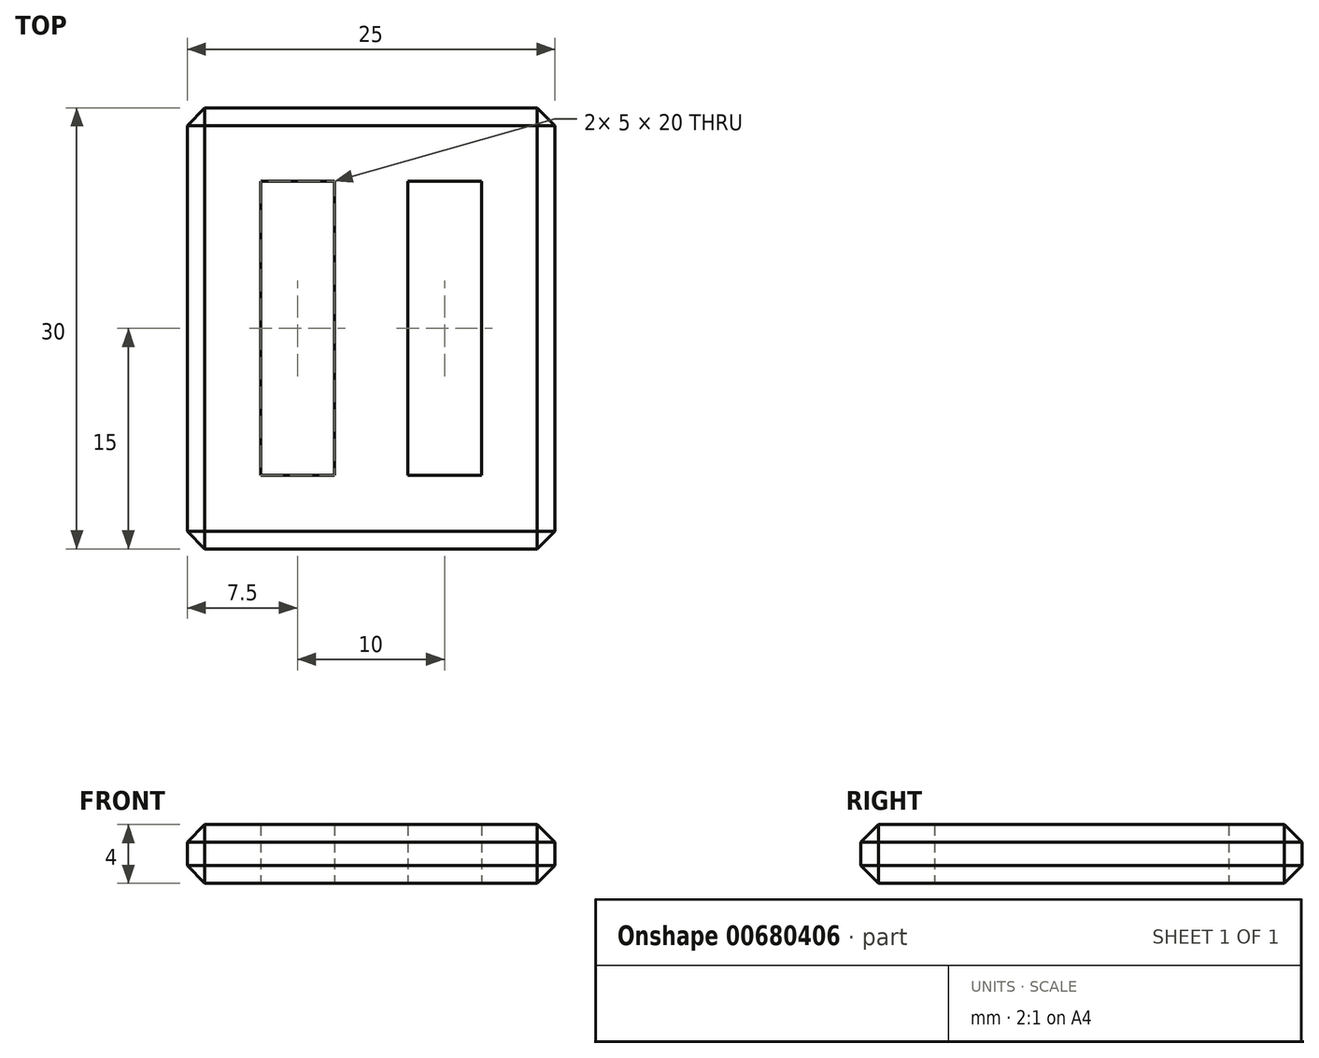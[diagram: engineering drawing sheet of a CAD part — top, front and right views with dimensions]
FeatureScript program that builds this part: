
annotation { "Feature Type Name" : "Feature", "Feature Type Description" : "" }
export const myFeature = defineFeature(function(context is Context, id is Id, definition is map)
    precondition{}
    {
        {
            var Q0;
            Q0=qCreatedBy(makeId("Top.planeOp"),FACE);
            var sketch = newSketch(context, id + "F0", { "sketchPlane" : qUnion([Q0])});
            skLineSegment(sketch, "E0.bottom", {"start": v(0, 0) * mm, "end": v(25, 0) * mm});
            skLineSegment(sketch, "E0.top", {"start": v(0, 30) * mm, "end": v(25, 30) * mm});
            skLineSegment(sketch, "E0.left", {"start": v(0, 0) * mm, "end": v(0, 30) * mm});
            skLineSegment(sketch, "E0.right", {"start": v(25, 0) * mm, "end": v(25, 30) * mm});
            skLineSegment(sketch, "E1.bottom", {"start": v(5, 5) * mm, "end": v(10, 5) * mm});
            skLineSegment(sketch, "E1.top", {"start": v(5, 25) * mm, "end": v(10, 25) * mm});
            skLineSegment(sketch, "E1.left", {"start": v(5, 5) * mm, "end": v(5, 25) * mm});
            skLineSegment(sketch, "E1.right", {"start": v(10, 5) * mm, "end": v(10, 25) * mm});
            skLineSegment(sketch, "E2.bottom", {"start": v(15, 5) * mm, "end": v(20, 5) * mm});
            skLineSegment(sketch, "E2.top", {"start": v(15, 25) * mm, "end": v(20, 25) * mm});
            skLineSegment(sketch, "E2.left", {"start": v(15, 5) * mm, "end": v(15, 25) * mm});
            skLineSegment(sketch, "E2.right", {"start": v(20, 5) * mm, "end": v(20, 25) * mm});
            skSolve(sketch);
        }
        {
            var Q0;
            Q0=makeQuery(id+"F0.imprint","IMPRINT",FACE,{"disambiguationData":[TD([[makeQuery(id+"F0.imprint","IMPRINT",EDGE,{"derivedFrom":sQuery(id+"F0.wireOp",EDGE,"E0.bottom")}),1.0]])]});
            extrude(context, id + "F1", {"entities" : qUnion([Q0]), "depth" : 4 * mm, "offsetDistance" : 25 * mm});
        }
        {
            var Q0;
            Q0=makeQuery(id+"F1.opExtrude","CAP_EDGE",EDGE,{"disambiguationData":[OSD([sQuery(id+"F0.wireOp",EDGE,"E0.top")])],"isStart":false});
            var Q1;
            Q1=makeQuery(id+"F1.opExtrude","CAP_EDGE",EDGE,{"disambiguationData":[OSD([sQuery(id+"F0.wireOp",EDGE,"E0.right")])],"isStart":false});
            var Q2;
            Q2=makeQuery(id+"F1.opExtrude","CAP_EDGE",EDGE,{"disambiguationData":[OSD([sQuery(id+"F0.wireOp",EDGE,"E0.bottom")])],"isStart":false});
            var Q3;
            Q3=makeQuery(id+"F1.opExtrude","CAP_EDGE",EDGE,{"disambiguationData":[OSD([sQuery(id+"F0.wireOp",EDGE,"E0.left")])],"isStart":false});
            var Q4;
            Q4=makeQuery(id+"F1.opExtrude","CAP_EDGE",EDGE,{"disambiguationData":[OSD([sQuery(id+"F0.wireOp",EDGE,"E0.right")])],"isStart":true});
            var Q5;
            Q5=makeQuery(id+"F1.opExtrude","CAP_EDGE",EDGE,{"disambiguationData":[OSD([sQuery(id+"F0.wireOp",EDGE,"E0.top")])],"isStart":true});
            var Q6;
            Q6=makeQuery(id+"F1.opExtrude","CAP_EDGE",EDGE,{"disambiguationData":[OSD([sQuery(id+"F0.wireOp",EDGE,"E0.bottom")])],"isStart":true});
            var Q7;
            Q7=makeQuery(id+"F1.opExtrude","CAP_EDGE",EDGE,{"disambiguationData":[OSD([sQuery(id+"F0.wireOp",EDGE,"E0.left")])],"isStart":true});
            var Q8;
            Q8=makeQuery(id+"F1.opExtrude","SWEPT_EDGE",EDGE,{"disambiguationData":[OSD([sQuery(id+"F0.wireOp",EDGE,"E0.top"),sQuery(id+"F0.wireOp",EDGE,"E0.right")])]});
            var Q9;
            Q9=makeQuery(id+"F1.opExtrude","SWEPT_EDGE",EDGE,{"disambiguationData":[OSD([sQuery(id+"F0.wireOp",EDGE,"E0.bottom"),sQuery(id+"F0.wireOp",EDGE,"E0.right")])]});
            var Q10;
            Q10=makeQuery(id+"F1.opExtrude","SWEPT_EDGE",EDGE,{"disambiguationData":[OSD([sQuery(id+"F0.wireOp",EDGE,"E0.top"),sQuery(id+"F0.wireOp",EDGE,"E0.left")])]});
            var Q11;
            Q11=makeQuery(id+"F1.opExtrude","SWEPT_EDGE",EDGE,{"disambiguationData":[OSD([sQuery(id+"F0.wireOp",EDGE,"E0.bottom"),sQuery(id+"F0.wireOp",EDGE,"E0.left")])]});
            chamfer(context, id + "F2", {"entities" : qUnion([Q0, Q1, Q2, Q3, Q4, Q5, Q6, Q7, Q8, Q9, Q10, Q11]), "width" : 1.2 * mm, "tangentPropagation" : true});
        }
    });
